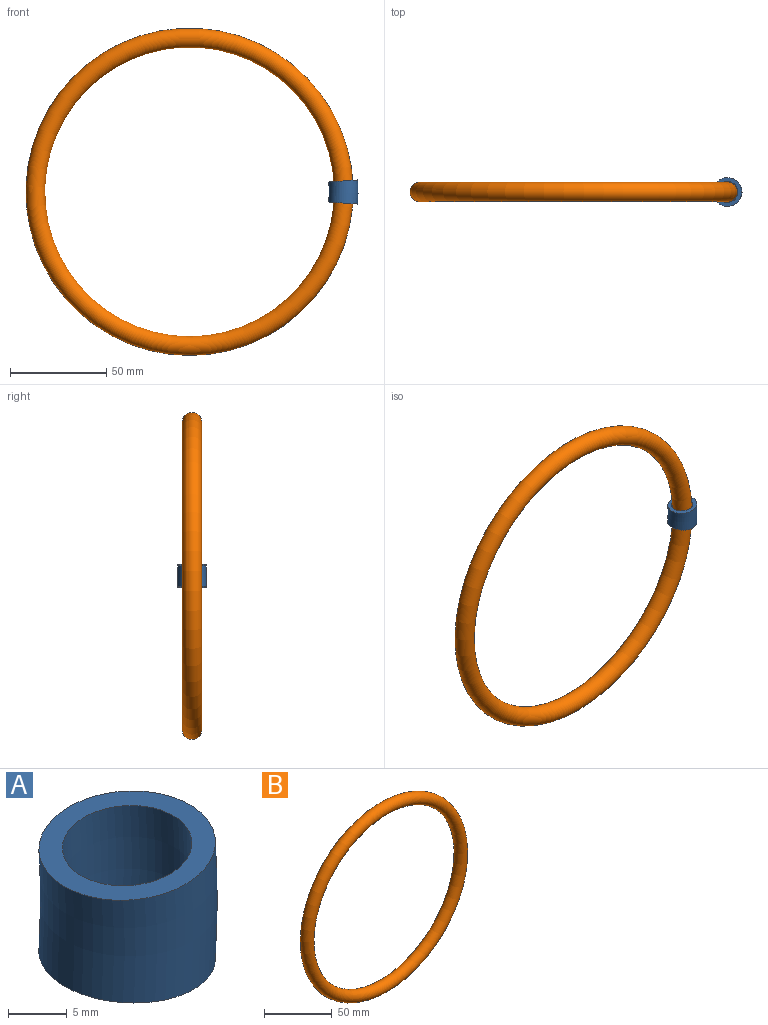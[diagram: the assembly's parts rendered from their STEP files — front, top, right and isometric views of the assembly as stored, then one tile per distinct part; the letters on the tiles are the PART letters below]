
ASSEMBLY  parts=2 mates=1
PART A: 4 faces, bbox 15.4x15x12.5 mm
  f0: plane 15x14.96mm, normal (-0.07,0,1), area 81.7mm2, adj f2,f3
  f1: plane 15x14.96mm, normal (-0.07,0,-1), area 81.7mm2, adj f2,f3
  f2: torus R=80mm, axis (0,-1,0), area 538.4mm2, adj f0,f1
  f3: torus R=80mm, axis (0,-1,0), area 394.8mm2, adj f0,f1
PART B: 1 faces, bbox 184x10x184 mm
  f0: torus R=80mm, axis (0,-1,0), area 15791.4mm2
PLACE A at identity
PLACE B at identity
MATE revolute A.f2 <-> B.f0  axis (0,-1,0) through (0,0,0)mm
